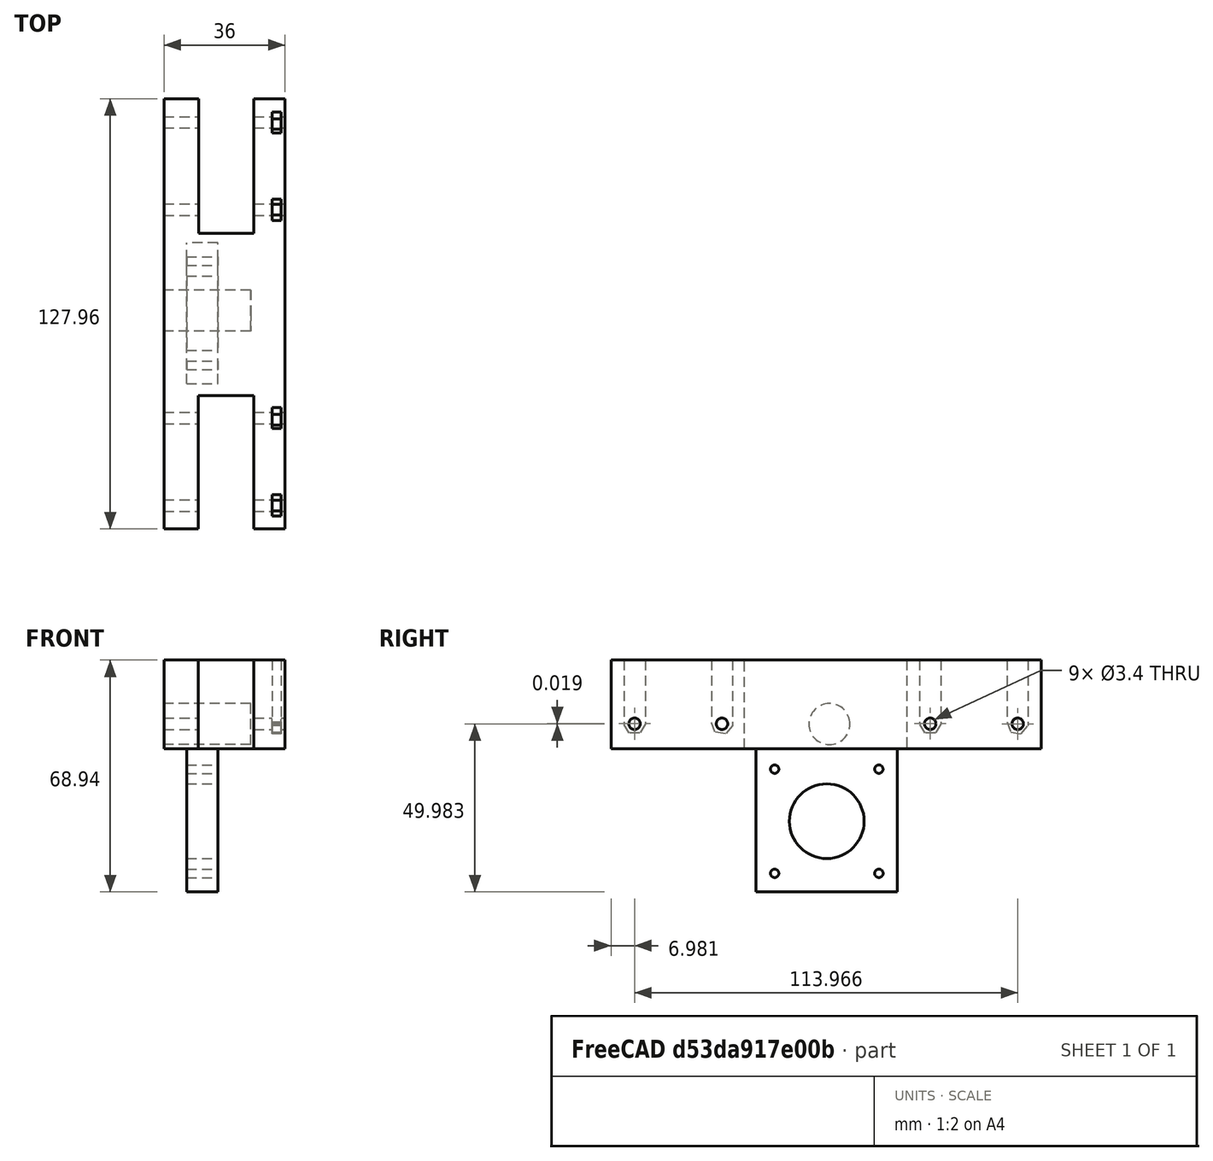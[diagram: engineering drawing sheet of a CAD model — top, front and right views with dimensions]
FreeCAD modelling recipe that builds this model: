
FCSTD DOCUMENT  (FreeCAD 2024.1R35694 (Git))
Label: Leadscrew_mount_back
License: All rights reserved
LicenseURL: http://en.wikipedia.org/wiki/All_rights_reserved
objects: PartDesign::Pocket×4, Part::Feature×1, PartDesign::FeatureBase×1, PartDesign::Body×1
note: 11 computed .brp shape members not serialized (recipe doc carries the construction recipe); baked Part::Feature solids carry a one-line shape summary decoded from their .brp

FEATURE [Part::Feature] Solid  label="Leadscrew_mount_back_001"
  shape: bbox 36 x 128 x 68.94 mm, 70 faces (baked)
FEATURE [PartDesign::FeatureBase] BaseFeature
  BaseFeature = -> Solid
FEATURE [PartDesign::Pocket] Pocket
  BaseFeature = -> BaseFeature
  Direction = (0,0,1)
  Length = 0.2
  Length2 = 5
  Profile = -> BaseFeature [Face52]
  Refine = true
  Type = 0
FEATURE [PartDesign::Pocket] Pocket001
  BaseFeature = -> Pocket
  Direction = (0,0,1)
  Length = 1
  Length2 = 5
  Profile = -> Pocket [Face1]
  Refine = true
  Type = 0
FEATURE [PartDesign::Pocket] Pocket002
  BaseFeature = -> Pocket001
  Direction = (0,0,1)
  Length = 0.5
  Length2 = 5
  Profile = -> Pocket001 [Face1]
  Refine = true
  Type = 0
FEATURE [PartDesign::Pocket] Pocket003
  BaseFeature = -> Pocket002
  Direction = (-1,0,0)
  Length = 0.3
  Length2 = 5
  Profile = -> Pocket002 [Face34,Face38,Face42,Face31]
  Refine = true
  Type = 0
FEATURE [PartDesign::Body] Body
  BaseFeature = -> Solid
  Group = -> [BaseFeature,Pocket,Pocket001,Pocket002,Pocket003]
  Origin = -> Origin
  Tip = -> Pocket003
